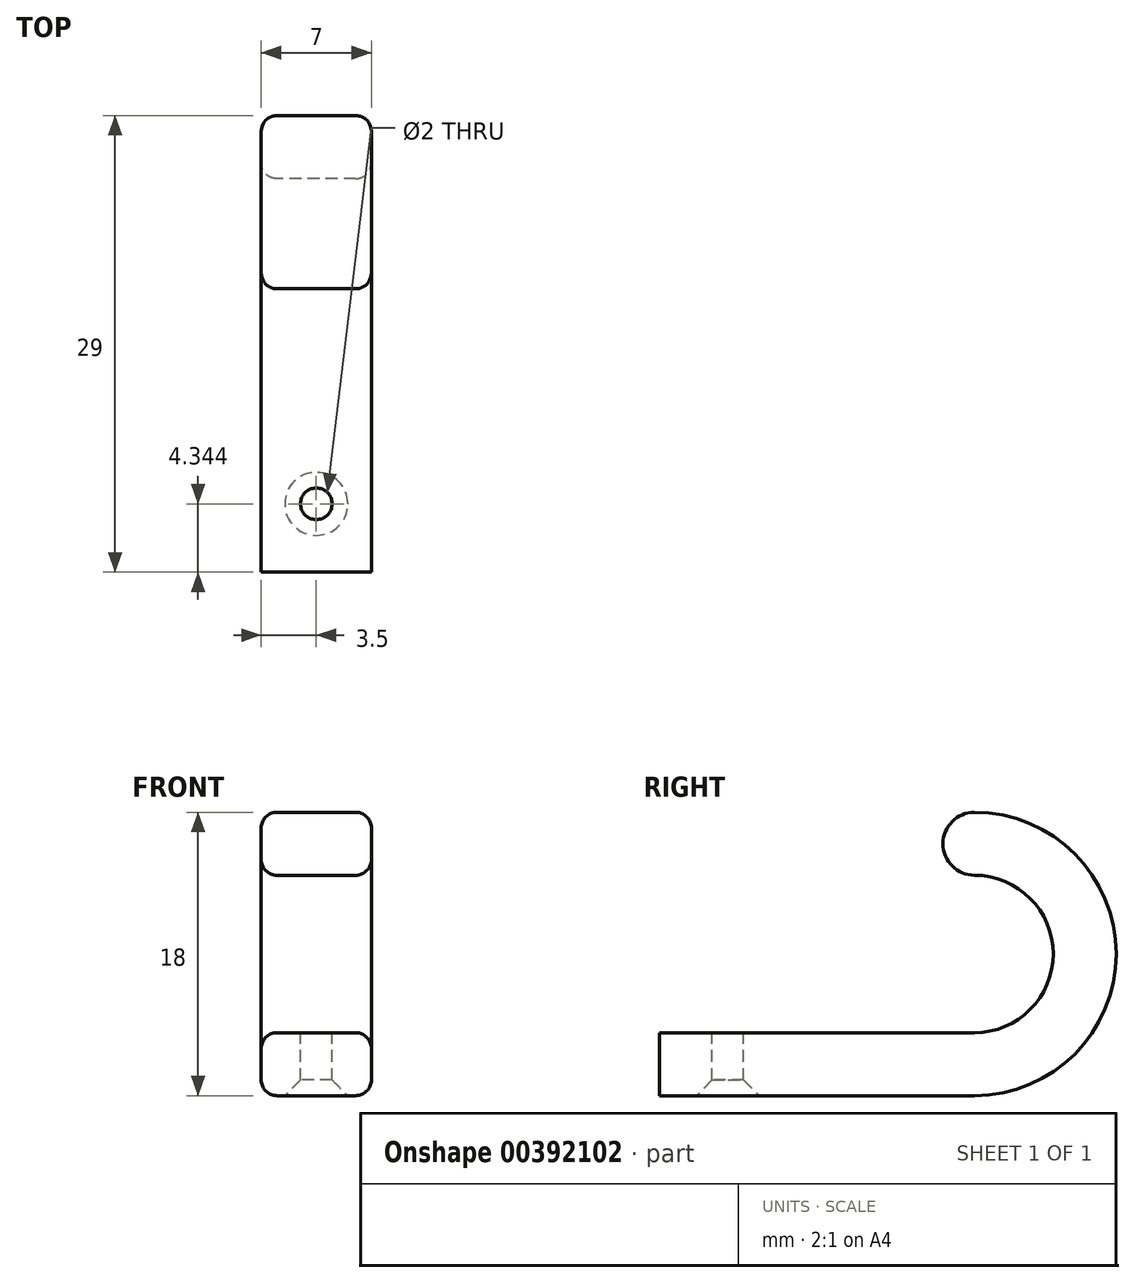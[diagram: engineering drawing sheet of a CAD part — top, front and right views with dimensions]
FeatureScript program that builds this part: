
annotation { "Feature Type Name" : "Feature", "Feature Type Description" : "" }
export const myFeature = defineFeature(function(context is Context, id is Id, definition is map)
    precondition{}
    {
        {
            var Q0;
            Q0=qCreatedBy(makeId("Right.planeOp"),FACE);
            var sketch = newSketch(context, id + "F0", { "sketchPlane" : qUnion([Q0])});
            skLineSegment(sketch, "E0", {"start": v(-59.78, 0) * mm, "end": v(-39.78, 0) * mm});
            skArc(sketch, "E1", {"start": v(-39.78, 0) * mm, "mid": v(-34.78, 5) * mm, "end": v(-39.78, 10) * mm});
            skArc(sketch, "E2.0", {"start": v(-39.78, -4) * mm, "mid": v(-30.78, 5) * mm, "end": v(-39.78, 14) * mm});
            skLineSegment(sketch, "E2.1", {"start": v(-59.78, -4) * mm, "end": v(-39.78, -4) * mm});
            skArc(sketch, "E3", {"start": v(-39.78, 14) * mm, "mid": v(-41.78, 12) * mm, "end": v(-39.78, 10) * mm});
            skLineSegment(sketch, "E4", {"start": v(-59.78, 0) * mm, "end": v(-59.78, -4) * mm});
            skSolve(sketch);
        }
        {
            var Q0;
            Q0=makeQuery(id+"F0.imprint","IMPRINT",FACE,{"disambiguationData":[TD([[makeQuery(id+"F0.imprint","IMPRINT",EDGE,{"derivedFrom":sQuery(id+"F0.wireOp",EDGE,"E0")}),-1.0]])]});
            extrude(context, id + "F1", {"entities" : qUnion([Q0]), "depth" : 7 * mm});
        }
        {
            var Q0;
            Q0=makeQuery(id+"F1.opExtrude","SWEPT_FACE",FACE,{"disambiguationData":[OSD([sQuery(id+"F0.wireOp",EDGE,"E0")])]});
            var sketch = newSketch(context, id + "F2", { "sketchPlane" : qUnion([Q0])});
            skLineSegment(sketch, "E5", {"start": v(0, -55.44) * mm, "end": v(7, -55.44) * mm, "construction": true});
            skLineSegment(sketch, "E6", {"start": v(3.5, -59.78) * mm, "end": v(3.5, -39.78) * mm, "construction": true});
            skCircle(sketch, "E7", {"center": v(3.5, -55.44) * mm, "radius": 1 * mm});
            skSolve(sketch);
        }
        {
            var Q0;
            Q0=makeQuery(id+"F2.imprint","IMPRINT",FACE,{"disambiguationData":[TD([[makeQuery(id+"F2.imprint","IMPRINT",EDGE,{"derivedFrom":sQuery(id+"F2.wireOp",EDGE,"E7")}),1.0]])]});
            var Q1;
            Q1=sQuery(id+"F2.wireOp",EDGE,"E7");
            extrude(context, id + "F3", {"entities" : qUnion([Q0]), "operationType" : NewBodyOperationType.REMOVE, "surfaceEntities" : qUnion([Q1]), "oppositeDirection" : true, "depth" : 25 * mm});
        }
        {
            var Q0;
            Q0=makeQuery(id+"F3.boolean.opBoolean","COPY",EDGE,{"derivedFrom":makeQuery(id+"F3.opExtrude","CAP_EDGE",EDGE,{"disambiguationData":[OSD([sQuery(id+"F2.wireOp",EDGE,"E7")])],"isStart":true})});
            var Q1;
            Q1=makeQuery(id+"F3.boolean.opBoolean","INTERSECT",EDGE,{"derivedFrom":[makeQuery(id+"F1.opExtrude","SWEPT_FACE",FACE,{"disambiguationData":[OSD([sQuery(id+"F0.wireOp",EDGE,"E2.1")])]}),makeQuery(id+"F3.opExtrude","SWEPT_FACE",FACE,{"disambiguationData":[OSD([sQuery(id+"F2.wireOp",EDGE,"E7")])]})]});
            chamfer(context, id + "F4", {"entities" : qUnion([Q0, Q1]), "width" : 1 * mm, "tangentPropagation" : true});
        }
        {
            var Q0;
            Q0=makeQuery(id+"F1.opExtrude","CAP_EDGE",EDGE,{"disambiguationData":[OSD([sQuery(id+"F0.wireOp",EDGE,"E0")])],"isStart":false});
            var Q1;
            Q1=makeQuery(id+"F1.opExtrude","CAP_EDGE",EDGE,{"disambiguationData":[OSD([sQuery(id+"F0.wireOp",EDGE,"E1")])],"isStart":false});
            var Q2;
            Q2=makeQuery(id+"F1.opExtrude","CAP_EDGE",EDGE,{"disambiguationData":[OSD([sQuery(id+"F0.wireOp",EDGE,"E0")])],"isStart":true});
            var Q3;
            Q3=makeQuery(id+"F1.opExtrude","CAP_EDGE",EDGE,{"disambiguationData":[OSD([sQuery(id+"F0.wireOp",EDGE,"E1")])],"isStart":true});
            fillet(context, id + "F5", {"entities" : qUnion([Q0, Q1, Q2, Q3]), "radius" : 1 * mm, "tangentPropagation" : true, "allowEdgeOverflow" : false});
        }
    });
